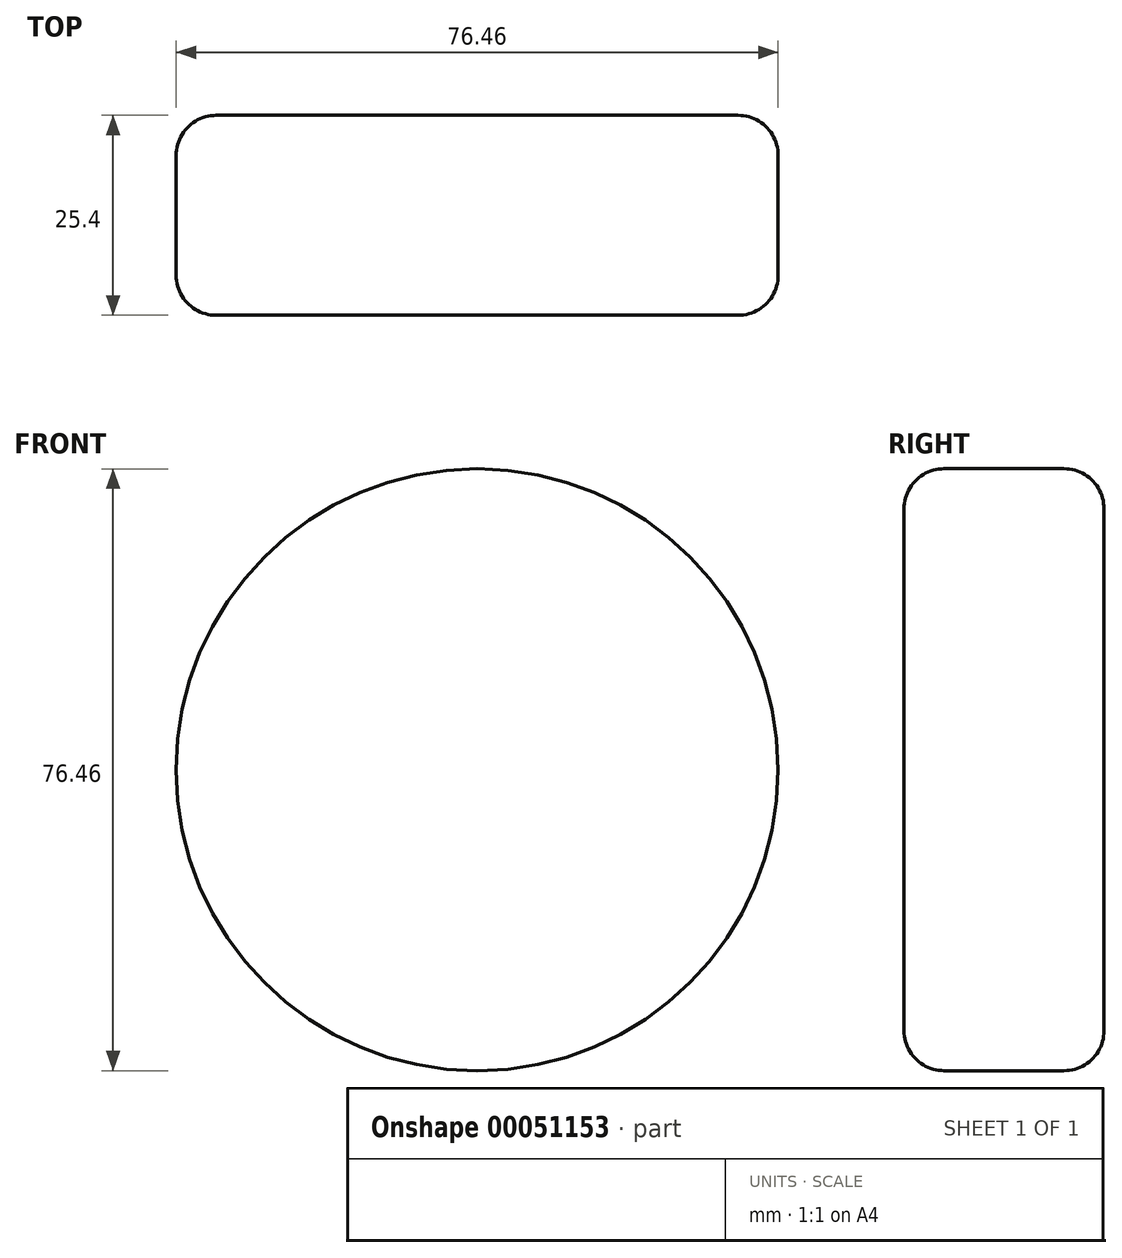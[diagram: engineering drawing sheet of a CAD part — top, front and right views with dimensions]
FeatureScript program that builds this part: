
annotation { "Feature Type Name" : "Feature", "Feature Type Description" : "" }
export const myFeature = defineFeature(function(context is Context, id is Id, definition is map)
    precondition{}
    {
        {
            var Q0;
            Q0=qCreatedBy(makeId("Front.planeOp"),FACE);
            var sketch = newSketch(context, id + "F0", { "sketchPlane" : qUnion([Q0])});
            skCircle(sketch, "E0", {"center": v(0, 0) * mm, "radius": 38.23 * mm});
            skSolve(sketch);
        }
        {
            var Q0;
            Q0=makeQuery(id+"F0.imprint","IMPRINT",FACE,{"disambiguationData":[TD([[makeQuery(id+"F0.imprint","IMPRINT",EDGE,{"derivedFrom":sQuery(id+"F0.wireOp",EDGE,"E0")}),1.0]])]});
            extrude(context, id + "F1", {"entities" : qUnion([Q0]), "depth" : 25.4 * mm});
        }
        {
            var Q0;
            Q0=makeQuery(id+"F1.opExtrude","CAP_EDGE",EDGE,{"disambiguationData":[OSD([sQuery(id+"F0.wireOp",EDGE,"E0")])],"isStart":false});
            var Q1;
            Q1=makeQuery(id+"F1.opExtrude","CAP_EDGE",EDGE,{"disambiguationData":[OSD([sQuery(id+"F0.wireOp",EDGE,"E0")])],"isStart":true});
            fillet(context, id + "F2", {"entities" : qUnion([Q0, Q1]), "radius" : 5.08 * mm, "tangentPropagation" : true, "allowEdgeOverflow" : false});
        }
    });
